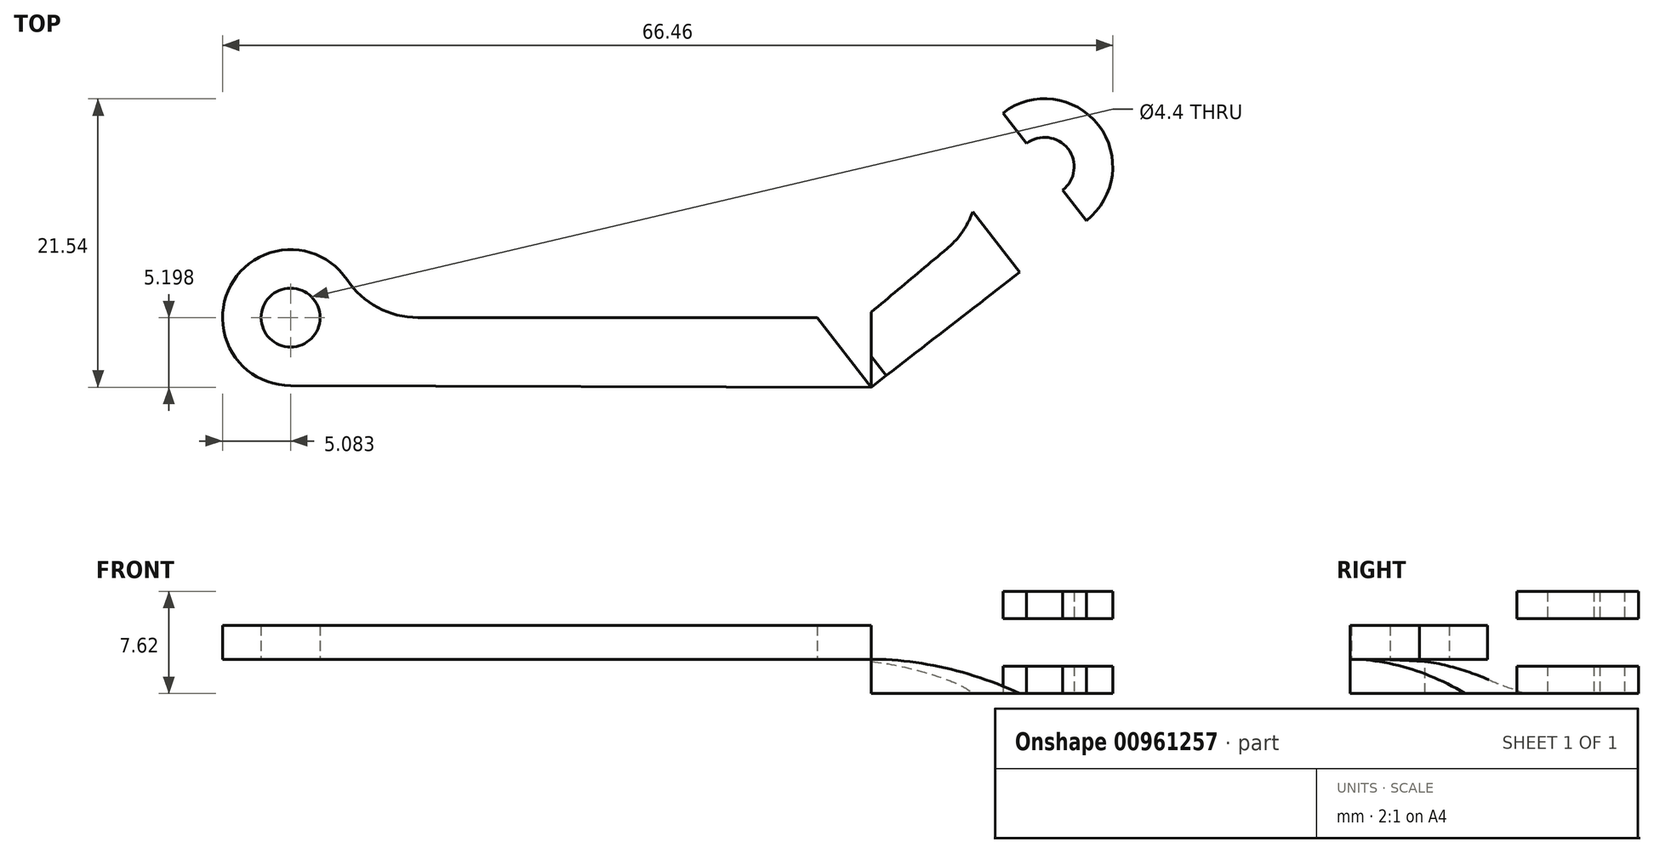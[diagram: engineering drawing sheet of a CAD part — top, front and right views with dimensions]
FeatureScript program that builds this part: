
annotation { "Feature Type Name" : "Feature", "Feature Type Description" : "" }
export const myFeature = defineFeature(function(context is Context, id is Id, definition is map)
    precondition{}
    {
        {
            var Q0;
            Q0=qCreatedBy(makeId("Top.planeOp"),FACE);
            var sketch = newSketch(context, id + "F0", { "sketchPlane" : qUnion([Q0])});
            skLineSegment(sketch, "E0.bottom", {"start": v(39.68, -27.9) * mm, "end": v(5.94, -27.8) * mm});
            skPoint(sketch, "E1.visualSharp", {"position": v(1.51, -27.8) * mm});
            skArc(sketch, "E2", {"start": v(0.56, -19.88) * mm, "mid": v(-8.15, -20.3) * mm, "end": v(-3.67, -27.78) * mm});
            skLineSegment(sketch, "E3", {"start": v(5.94, -27.8) * mm, "end": v(-3.67, -27.78) * mm});
            skPoint(sketch, "E4.visualSharp", {"position": v(1.41, -22.7) * mm});
            skArc(sketch, "E4.filletArc", {"start": v(0.56, -19.88) * mm, "mid": v(2.84, -21.95) * mm, "end": v(5.84, -22.7) * mm});
            skCircle(sketch, "E5", {"center": v(-3.67, -22.7) * mm, "radius": 2.2 * mm});
            skLineSegment(sketch, "E6", {"start": v(39.2, -22.7) * mm, "end": v(45.35, -17.55) * mm});
            skLineSegment(sketch, "E7", {"start": v(39.68, -27.9) * mm, "end": v(55.74, -15.45) * mm});
            skArc(sketch, "E8", {"start": v(55.74, -15.45) * mm, "mid": v(54.61, -6.76) * mm, "end": v(47.58, -11.99) * mm});
            skLineSegment(sketch, "E9.trimOffspring", {"start": v(39.2, -22.7) * mm, "end": v(5.84, -22.7) * mm});
            skPoint(sketch, "E10.visualSharp", {"position": v(48.74, -14.7) * mm});
            skArc(sketch, "E10.filletArc", {"start": v(45.35, -17.55) * mm, "mid": v(47.16, -15.05) * mm, "end": v(47.58, -11.99) * mm});
            skCircle(sketch, "E11", {"center": v(52.63, -11.44) * mm, "radius": 2.2 * mm});
            skSolve(sketch);
        }
        {
            var Q0;
            Q0=makeQuery(id+"F0.imprint","IMPRINT",FACE,{"disambiguationData":[TD([[makeQuery(id+"F0.imprint","IMPRINT",EDGE,{"derivedFrom":sQuery(id+"F0.wireOp",EDGE,"E0.bottom")}),-1.0]])]});
            extrude(context, id + "F1", {"entities" : qUnion([Q0]), "depth" : 7.62 * mm, "offsetDistance" : 25.4 * mm});
        }
        {
            var Q0;
            Q0=makeQuery(id+"F1.opExtrude","SWEPT_FACE",FACE,{"disambiguationData":[OSD([sQuery(id+"F0.wireOp",EDGE,"E0.bottom")])]});
            var sketch = newSketch(context, id + "F2", { "sketchPlane" : qUnion([Q0])});
            skLineSegment(sketch, "E12.bottom", {"start": v(55.7, 7.62) * mm, "end": v(-12.19, 7.62) * mm});
            skLineSegment(sketch, "E12.top", {"start": v(55.7, 0) * mm, "end": v(-12.19, 0) * mm});
            skLineSegment(sketch, "E12.right", {"start": v(-12.19, 7.62) * mm, "end": v(-12.19, 0) * mm});
            skLineSegment(sketch, "E13.bottom", {"start": v(55.7, 5.08) * mm, "end": v(-12.19, 5.08) * mm});
            skLineSegment(sketch, "E13.top", {"start": v(55.7, 2.54) * mm, "end": v(-12.19, 2.54) * mm});
            skLineSegment(sketch, "E13.right", {"start": v(-12.19, 5.08) * mm, "end": v(-12.19, 2.54) * mm});
            skLineSegment(sketch, "E14", {"start": v(46.88, 7.62) * mm, "end": v(46.88, 0) * mm});
            skLineSegment(sketch, "E15", {"start": v(39.76, 7.62) * mm, "end": v(39.76, 0) * mm});
            skSolve(sketch);
        }
        {
            var Q0;
            {var subQ0=sQuery(id+"F2.wireOp",EDGE,"E12.top");var subQ3=sQuery(id+"F2.wireOp",EDGE,"E12.right");var subQ4=makeQuery(id+"F2.imprint","INTERSECT",VERTEX,{"derivedFrom":[subQ0,subQ3]});Q0=makeQuery(id+"F2.imprint","IMPRINT",FACE,{"disambiguationData":[TD([[makeQuery(id+"F2.imprint","IMPRINT",EDGE,{"disambiguationData":[TD([[subQ4,1.0]])],"derivedFrom":subQ3}),1.0]])]});}
            var Q1;
            {var subQ0=sQuery(id+"F2.wireOp",EDGE,"E15");var subQ1=sQuery(id+"F2.wireOp",EDGE,"E12.top");var subQ2=makeQuery(id+"F2.imprint","INTERSECT",VERTEX,{"derivedFrom":[subQ1,subQ0]});Q1=makeQuery(id+"F2.imprint","IMPRINT",FACE,{"disambiguationData":[TD([[makeQuery(id+"F2.imprint","IMPRINT",EDGE,{"disambiguationData":[TD([[subQ2,1.0]])],"derivedFrom":subQ0}),-1.0]])]});}
            var Q2;
            {var subQ0=sQuery(id+"F2.wireOp",EDGE,"E12.bottom");var subQ3=sQuery(id+"F2.wireOp",EDGE,"E12.right");var subQ4=makeQuery(id+"F2.imprint","INTERSECT",VERTEX,{"derivedFrom":[subQ0,subQ3]});Q2=makeQuery(id+"F2.imprint","IMPRINT",FACE,{"disambiguationData":[TD([[makeQuery(id+"F2.imprint","IMPRINT",EDGE,{"disambiguationData":[TD([[subQ4,-1.0]])],"derivedFrom":subQ3}),1.0]])]});}
            var Q3;
            {var subQ0=sQuery(id+"F2.wireOp",EDGE,"E15");var subQ1=sQuery(id+"F2.wireOp",EDGE,"E12.bottom");var subQ2=makeQuery(id+"F2.imprint","INTERSECT",VERTEX,{"derivedFrom":[subQ1,subQ0]});Q3=makeQuery(id+"F2.imprint","IMPRINT",FACE,{"disambiguationData":[TD([[makeQuery(id+"F2.imprint","IMPRINT",EDGE,{"disambiguationData":[TD([[subQ2,-1.0]])],"derivedFrom":subQ0}),-1.0]])]});}
            extrude(context, id + "F3", {"entities" : qUnion([Q0, Q1, Q2, Q3]), "operationType" : NewBodyOperationType.REMOVE, "oppositeDirection" : true, "depth" : 25.4 * mm, "offsetDistance" : 25.4 * mm, "symmetric" : true});
        }
        {
            var Q0;
            Q0=makeQuery(id+"F1.opExtrude","SWEPT_FACE",FACE,{"disambiguationData":[OSD([sQuery(id+"F0.wireOp",EDGE,"E7")])]});
            var sketch = newSketch(context, id + "F4", { "sketchPlane" : qUnion([Q0])});
            skLineSegment(sketch, "E16", {"start": v(46.24, 5.08) * mm, "end": v(42.24, 5.08) * mm});
            skArc(sketch, "E17", {"start": v(15.68, 5.08) * mm, "mid": v(22.08, 5.88) * mm, "end": v(28.28, 7.62) * mm});
            skLineSegment(sketch, "E18", {"start": v(29.56, 5.08) * mm, "end": v(29.56, 5.58) * mm});
            skLineSegment(sketch, "E19", {"start": v(29.56, 5.58) * mm, "end": v(41.7, 5.58) * mm});
            skLineSegment(sketch, "E20", {"start": v(28.28, 7.62) * mm, "end": v(42.24, 7.62) * mm});
            skLineSegment(sketch, "E21", {"start": v(42.24, 7.62) * mm, "end": v(42.24, 5.08) * mm});
            skLineSegment(sketch, "E22", {"start": v(41.7, 5.58) * mm, "end": v(42.24, 5.58) * mm});
            skPoint(sketch, "E23.trimOffspring.end.orphan", {"position": v(34.59, 5.08) * mm});
            skLineSegment(sketch, "E24", {"start": v(15.68, 5.08) * mm, "end": v(14.27, 5.08) * mm});
            skLineSegment(sketch, "E25", {"start": v(14.27, 5.08) * mm, "end": v(14.27, 7.62) * mm});
            skLineSegment(sketch, "E26", {"start": v(14.27, 7.62) * mm, "end": v(28.28, 7.62) * mm});
            skLineSegment(sketch, "E27", {"start": v(29.56, 5.08) * mm, "end": v(29.56, 4.3) * mm});
            skLineSegment(sketch, "E28", {"start": v(42.24, 5.08) * mm, "end": v(42.24, 3.4) * mm});
            skLineSegment(sketch, "E29", {"start": v(14.27, 3.81) * mm, "end": v(20.12, 3.81) * mm, "construction": true});
            skArc(sketch, "E30.MirrorCS", {"start": v(15.68, 2.54) * mm, "mid": v(22.08, 1.74) * mm, "end": v(28.28, 0) * mm});
            skLineSegment(sketch, "E31.MirrorCS", {"start": v(14.27, 0) * mm, "end": v(28.28, 0) * mm});
            skLineSegment(sketch, "E32.MirrorCS", {"start": v(14.27, 2.54) * mm, "end": v(14.27, 0) * mm});
            skLineSegment(sketch, "E33.MirrorCS", {"start": v(15.68, 2.54) * mm, "end": v(14.27, 2.54) * mm});
            skLineSegment(sketch, "E34.MirrorCS", {"start": v(29.56, 2.04) * mm, "end": v(41.7, 2.04) * mm});
            skLineSegment(sketch, "E35.MirrorCS", {"start": v(28.28, 0) * mm, "end": v(42.24, 0) * mm});
            skLineSegment(sketch, "E36.MirrorCS", {"start": v(29.56, 2.54) * mm, "end": v(29.56, 3.32) * mm});
            skLineSegment(sketch, "E37.MirrorCS", {"start": v(29.56, 2.54) * mm, "end": v(29.56, 2.04) * mm});
            skLineSegment(sketch, "E38.MirrorCS", {"start": v(42.24, 0) * mm, "end": v(42.24, 2.54) * mm});
            skLineSegment(sketch, "E39.MirrorCS", {"start": v(42.24, 2.54) * mm, "end": v(42.24, 4.22) * mm});
            skLineSegment(sketch, "E40.MirrorCS", {"start": v(41.7, 2.04) * mm, "end": v(42.24, 2.04) * mm});
            skLineSegment(sketch, "E41", {"start": v(29.56, 4.3) * mm, "end": v(29.56, 3.32) * mm});
            skSolve(sketch);
        }
        {
            var Q0;
            Q0=makeQuery(id+"F4.imprint","IMPRINT",FACE,{"disambiguationData":[TD([[makeQuery(id+"F4.imprint","IMPRINT",EDGE,{"derivedFrom":sQuery(id+"F4.wireOp",EDGE,"E17")}),1.0]])]});
            var Q1;
            {var subQ4=sQuery(id+"F4.wireOp",EDGE,"E18");Q1=makeQuery(id+"F4.imprint","IMPRINT",FACE,{"disambiguationData":[TD([[makeQuery(id+"F4.imprint","IMPRINT",EDGE,{"derivedFrom":subQ4}),-1.0]])]});}
            var Q2;
            {var subQ2=sQuery(id+"F4.wireOp",EDGE,"E22");Q2=makeQuery(id+"F4.imprint","IMPRINT",FACE,{"disambiguationData":[TD([[makeQuery(id+"F4.imprint","IMPRINT",EDGE,{"derivedFrom":subQ2}),-1.0]])]});}
            var Q3;
            Q3=makeQuery(id+"F4.imprint","IMPRINT",FACE,{"disambiguationData":[TD([[makeQuery(id+"F4.imprint","IMPRINT",EDGE,{"derivedFrom":sQuery(id+"F4.wireOp",EDGE,"E30.MirrorCS")}),-1.0]])]});
            extrude(context, id + "F5", {"entities" : qUnion([Q0, Q1, Q2, Q3]), "operationType" : NewBodyOperationType.REMOVE, "oppositeDirection" : true, "depth" : 25.4 * mm, "offsetDistance" : 25.4 * mm});
        }
    });
